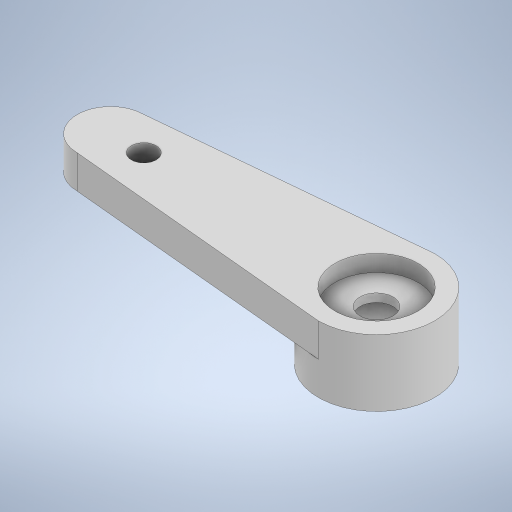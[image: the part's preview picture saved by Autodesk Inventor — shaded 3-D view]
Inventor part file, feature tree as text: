
AUTODESK INVENTOR PART (.ipt)
format: ipt  version: 2023.2 (Build 272271000, 271)  size: 297,984 bytes
history: native  units: mm
features: sketch x2
ambient origin geometry x8: Origin, YZ Plane, XZ Plane, XY Plane, X Axis, Y Axis, Z Axis, Center Point
bodies: Body1 (feature_tree)
feature tree (2):
  sketch  "Sketch2"  dims[d229=7.0mm d230=2.0mm d231=0.0mm d234=1.5mm d236=16.0mm d237=2.0mm d238=2.0mm d239=2.0mm d240=0.0mm d241=2.0mm d242=1.0mm d243=0.0mm d244=0.5mm d245=0.0mm d9=0.5mm d10=0.872665mm d11=0.5mm d12=0.872665mm d13=0.5mm d14=0.872665mm d27=0.5mm d28=0.872665mm d29=0.5mm d30=0.872665mm d88=0.5mm d89=0.872665mm d90=0.5mm d91=0.872665mm d116=0.5mm d117=0.872665mm d118=0.5mm d119=0.872665mm d154=0.5mm d155=0.872665mm d156=0.5mm d157=0.872665mm d181=0.5mm d182=0.872665mm d183=0.5mm d184=0.872665mm d221=0.5mm d222=0.872665mm d223=0.5mm d224=0.872665mm]
  sketch  "Sketch1"  dims[d228=5.0mm]
